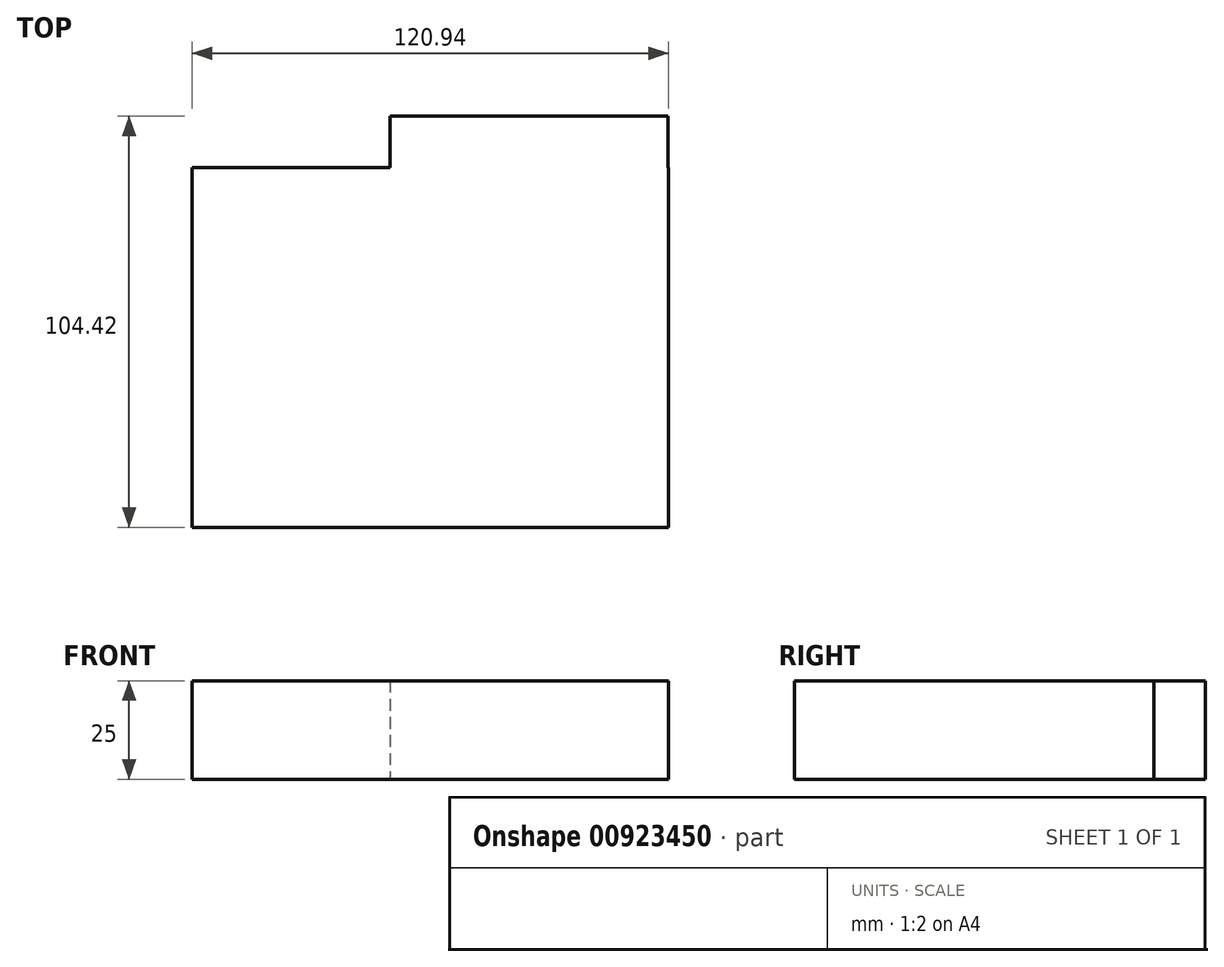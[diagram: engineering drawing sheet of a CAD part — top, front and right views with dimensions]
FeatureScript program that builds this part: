
annotation { "Feature Type Name" : "Feature", "Feature Type Description" : "" }
export const myFeature = defineFeature(function(context is Context, id is Id, definition is map)
    precondition{}
    {
        {
            var Q0;
            Q0=qCreatedBy(makeId("Top.planeOp"),FACE);
            var sketch = newSketch(context, id + "F0", { "sketchPlane" : qUnion([Q0])});
            skLineSegment(sketch, "E0.bottom", {"start": v(-60.47, 45.69) * mm, "end": v(60.47, 45.69) * mm});
            skLineSegment(sketch, "E0.top", {"start": v(-60.47, -45.69) * mm, "end": v(60.47, -45.69) * mm});
            skLineSegment(sketch, "E0.left", {"start": v(-60.47, 45.69) * mm, "end": v(-60.47, -45.69) * mm});
            skLineSegment(sketch, "E0.right", {"start": v(60.47, 45.69) * mm, "end": v(60.47, -45.69) * mm});
            skPoint(sketch, "E0.middle", {"position": v(0, 0) * mm});
            skSolve(sketch);
        }
        {
            var Q0;
            Q0=makeQuery(id+"F0.imprint","IMPRINT",FACE,{"disambiguationData":[TD([[makeQuery(id+"F0.imprint","IMPRINT",EDGE,{"derivedFrom":sQuery(id+"F0.wireOp",EDGE,"E0.bottom")}),-1.0]])]});
            var sketch = newSketch(context, id + "F1", { "sketchPlane" : qUnion([Q0])});
            skLineSegment(sketch, "E1", {"start": v(-10.22, 58.73) * mm, "end": v(60.37, 58.73) * mm});
            skLineSegment(sketch, "E2", {"start": v(60.37, 58.73) * mm, "end": v(60.37, -45.63) * mm});
            skLineSegment(sketch, "E3", {"start": v(60.37, -45.63) * mm, "end": v(-10.22, -45.63) * mm});
            skLineSegment(sketch, "E4", {"start": v(-10.22, -45.63) * mm, "end": v(-10.22, 58.73) * mm});
            skSolve(sketch);
        }
        {
            var Q0;
            {var subQ0=sQuery(id+"F1.wireOp",EDGE,"E1");Q0=makeQuery(id+"F1.imprint","IMPRINT",FACE,{"disambiguationData":[TD([[makeQuery(id+"F1.imprint","IMPRINT",EDGE,{"derivedFrom":subQ0}),-1.0]])]});}
            extrude(context, id + "F2", {"entities" : qUnion([Q0]), "depth" : 25 * mm, "offsetDistance" : 25 * mm});
        }
        {
            var Q0;
            Q0=makeQuery(id+"F0.imprint","IMPRINT",FACE,{"disambiguationData":[TD([[makeQuery(id+"F0.imprint","IMPRINT",EDGE,{"derivedFrom":sQuery(id+"F0.wireOp",EDGE,"E0.bottom")}),-1.0]])]});
            extrude(context, id + "F3", {"entities" : qUnion([Q0]), "operationType" : NewBodyOperationType.ADD, "depth" : 25 * mm, "offsetDistance" : 25 * mm});
        }
    });
